# Revit family: Geberit Sigma ugradni vodokotlić 8 cm, 6 _ 3 litara_PRO_168868
name_source: partatom
category: Plumbing Fixtures
units: mm (PartAtom-declared; Revit-internal decimal feet)

## family parameters
Always vertical = Yes
Cut with Voids When Loaded = No
OmniClass Number = 23.31.19.00
Part Type = Normal
Room Calculation Point = Yes
Round Connector Dimension = Use Diameter
Shared = No
Work Plane-Based = No

## types (1)
- 109.791.00.1 Geberit Sigma ugradni vodokotlić 8 cm, 6 / 3 litara
    B = 410 mm  [stored 1.34514 ft]
    BIM datoteka, datum izmene = 2023.07.05
    BIM datoteka, proizvođač = Geberit
    BIM datoteka, verzija = GEB MG 1.6
    Broj artikla = 109.791.00.1
    CW Connection = Yes
    D1 = 50 mm  [stored 0.164042 ft]
    Default Elevation = 0 mm  [stored 0 ft]
    Description = Geberit Sigma ugradni vodokotlić 8 cm, 6 / 3 litara
    EAN code basic data = 4025416351986
    Fabrički podešena količina ispiranja = 6 i 3 l
    GEB_culture = sr-RS
    GEB_generic_description = concealed cistern for toilet
    GEB_generic_manufacturer = generic
    GEB_imperial_engineering = No
    GEB_metric_engineering = Yes
    GEB_pimversion = 23.08.11
    GEB_processing_type = T
    GEB_reference = PRO_168868
    GEB_translations = {"application_range":"Oblast primene","applicationPurposes":"Namene","ATT_10673":"EAN code basic data","ATT_10773":"Protočni pritisak","ATT_10807":"Opseg podešavanje veće količine vode za ispiranje","ATT_10811":"Opseg podešavanja manje količine vode za ispiranje","ATT_10832":"Maksimalna temperatura vode","ATT_10866":"Fabrički podešena količina ispiranja","brandName":"Robna marka","characteristics":"Svojstva","connection_description1":"Opis priključka 1","connection_description2":"Opis priključka 2","connection_type_c01":"Vrsta priključka kod priključka 01","connection_type_c02":"Vrsta priključka kod priključka 02","content_creator":"BIM datoteka, proizvođač","content_date_changed":"BIM datoteka, datum izmene","content_version":"BIM datoteka, verzija","GEB_connection_diameter1":"Prečnik priključka 1","GEB_connection_diameter2":"Prečnik priključka 2","key 1000":"Broj artikla","name":"Naziv","productBrand":"Robna marka proizvoda","scopeOfDelivery":"Obim isporuke","type":"Tip","GEB_cut_length_c01":"Maksimalno skraćenje kod priključka 01","angle":"ugao","placement finished floor":"Na gornjoj ivici gotovog poda","sanitary socket":"Spojnica za prelaz","surface height":"Visina debljine poda","warning":"Upozorenje","fixed_material":"Osnovni materijal","fixed_material_01":"Osnovni materijal 01","fixed_material_03":"Osnovni materijal 03","ATT_10931":"B","ATT_10951":"H","ATT_380239":"T"}
    GEB_use_DN = Yes
    H = 625 mm  [stored 2.05052 ft]
    HW Connection = No
    IfcDescription = Geberit Sigma ugradni vodokotlić 8 cm, 6 / 3 litara
    IfcExportAs = IfcSanitaryTerminal
    IfcExportType = CISTERN
    LOD300 = No
    LOD400 = Yes
    Maksimalna temperatura vode = 25 °C
    Manufacturer = Geberit
    Model = Sigma 8 cm
    Namene = Za ozidane zidove
Za ugradnju u predzidne konstrukcije delimične ili visine etaže
Za ugradnju u instalacione zidove u visini etaže
Za podni WC
Za jednokoličinsko, dvokoličinsko ili start/stop ispiranje
    Naziv = Geberit Sigma ugradni vodokotlić 8 cm, 6 / 3 litara
    Obim isporuke = Priključak vode R 1/2", kompatibilan sa MF adapterom, sa integrisanim ugaonim ventilom i ručnim točkićem
Građevinska zaštita za revizioni otvor
Ispirno koleno sa izolacionom oblogama
Produžetak ispirnog kolena ø 45 mm
Zaštitni čep
2 čelične trake za pričvršćenje
Materijal za pričvršćivanje
    Oblast primene = sanitary systems
    Opis priključka 1 = cold water in
    Opis priključka 2 = sanitary out
    Opseg podešavanja manje količine vode za ispiranje = 2-4 l
    Opseg podešavanje veće količine vode za ispiranje = 4 / 4.5 / 6 / 7.5 l
    Osnovni materijal = Geberit, Plastic, Opaque white
    Osnovni materijal 01 = Geberit, Laminate, Ivory, Matte
    Osnovni materijal 03 = Geberit, PE-HD, Black
    Protočni pritisak = 0.1-10 bar
    Robna marka = Geberit
    Svojstva = Serija 2016.
Ugradni vodokotlić sa aktiviranjem sa prednje strane
Ugradni vodokotlić sa izolacijom protiv kondenzacije
Mreža za ojačanje maltera, predmontirana
Kod fabričkog podešavanja moguće je automatsko naknadno ispiranje
Ispirno koleno, sakriveno
Ispirno koleno sa mogućnošću pomeranja nagore 2 cm i nadole 1 cm
Radovi na montaži i servisu na ugradnom vodokotliću bez alata
Priključak za vodu sa gornje leve strane
Građevinska zaštita štiti otvor za servisiranje od vlage i prljavštine
Građevinska zaštita za revizioni otvor koja se može seći po dužini, odgovara za tipke za aktiviranje ravne sa zidom
    T = 80 mm  [stored 0.262467 ft]
    Tip = Sigma 8 cm
    Vent Connection = No
    Waste Connection = Yes
    cistern_bottom = 625 mm  [stored 2.05052 ft]
    cistern_depth = 80 mm  [stored 0.262467 ft]
    cistern_top_offset = 0 mm  [stored 0 ft]
    cistern_width = 410 mm  [stored 1.34514 ft]
    connection_bend = No
    flushing_water_pipe_D = 80 mm  [stored 0.262467 ft]
    outlet_flow = 0.0 L/s
    plastering_netting = Yes

note: [stored X ft] marks values corroborated as IEEE doubles in the binary element streams (Revit-internal decimal feet)

## geometry (parser evidence)
native form markers: Blend x4, Sweep x9
no freeform markers — native parametric forms only
